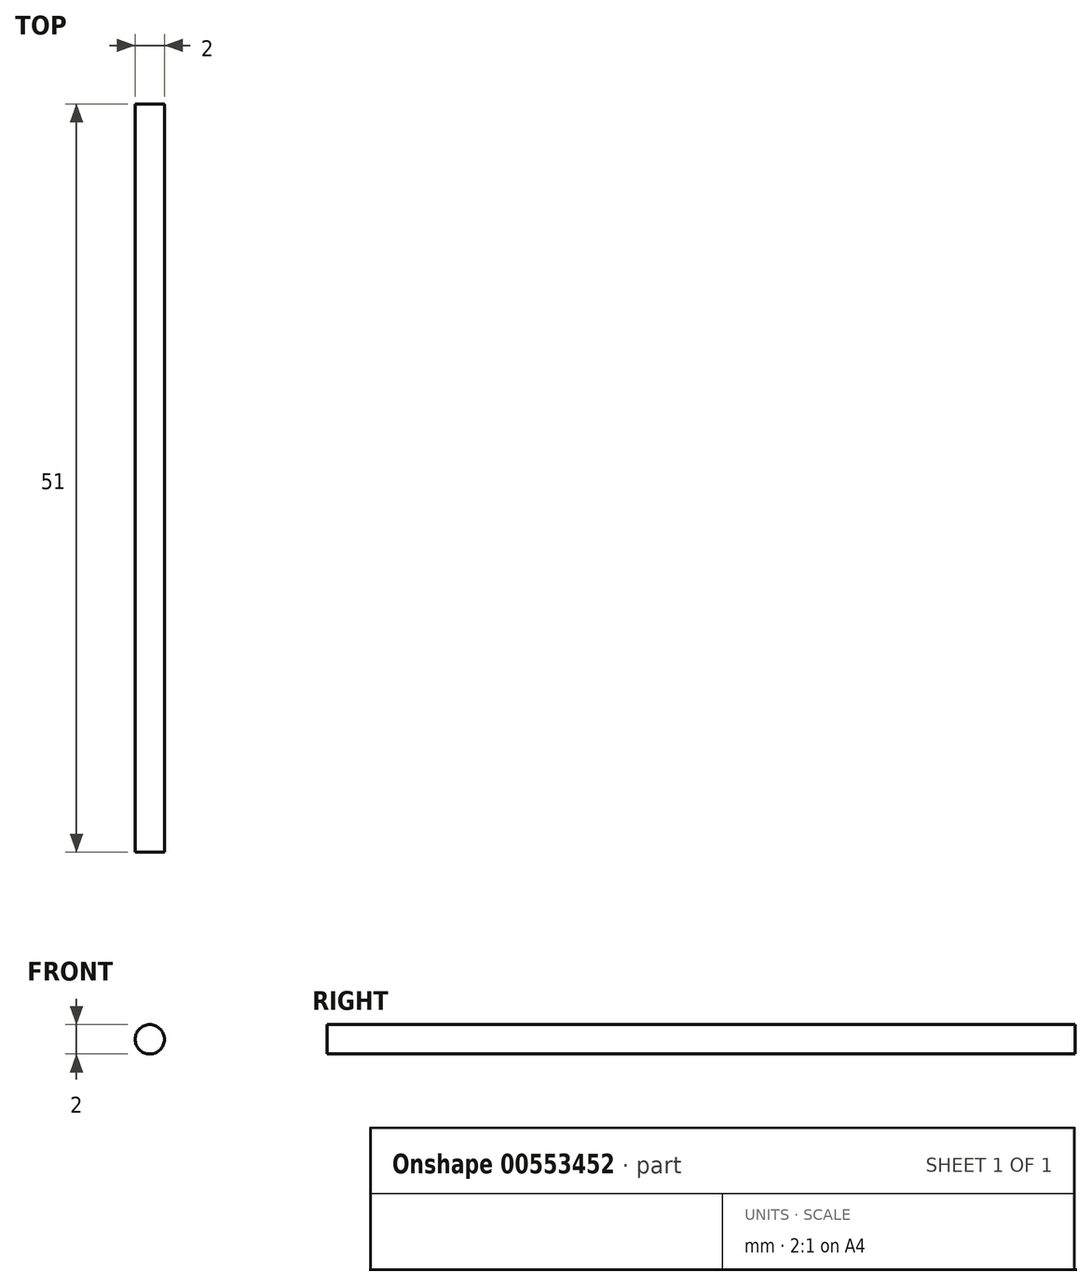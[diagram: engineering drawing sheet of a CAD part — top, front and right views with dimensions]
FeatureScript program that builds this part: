
annotation { "Feature Type Name" : "Feature", "Feature Type Description" : "" }
export const myFeature = defineFeature(function(context is Context, id is Id, definition is map)
    precondition{}
    {
        {
            var Q0;
            Q0=qCreatedBy(makeId("Front.planeOp"),FACE);
            var sketch = newSketch(context, id + "F0", { "sketchPlane" : qUnion([Q0])});
            skCircle(sketch, "E0", {"center": v(0, 0) * mm, "radius": 1 * mm});
            skSolve(sketch);
        }
        {
            var Q0;
            Q0 = qSketchRegion(id + "F0", true);
            extrude(context, id + "F1", {"entities" : qUnion([Q0]), "depth" : 51 * mm, "offsetDistance" : 25 * mm});
        }
    });
